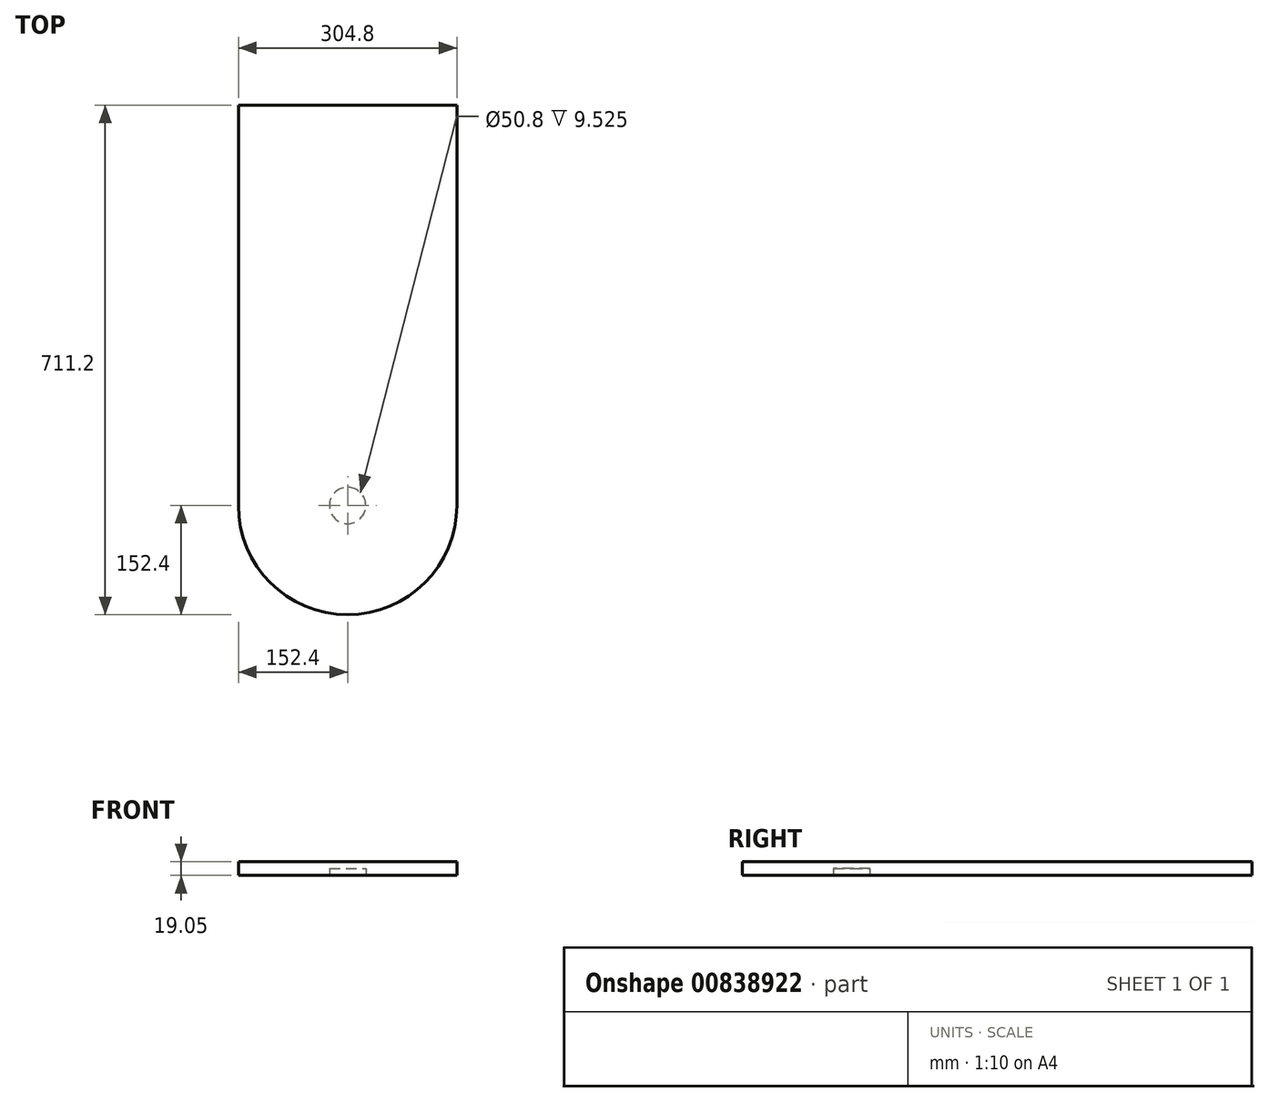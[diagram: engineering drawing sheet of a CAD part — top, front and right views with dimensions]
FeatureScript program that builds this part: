
annotation { "Feature Type Name" : "Feature", "Feature Type Description" : "" }
export const myFeature = defineFeature(function(context is Context, id is Id, definition is map)
    precondition{}
    {
        {
            var Q0;
            Q0=qCreatedBy(makeId("Top.planeOp"),FACE);
            var sketch = newSketch(context, id + "F0", { "sketchPlane" : qUnion([Q0])});
            skLineSegment(sketch, "E0", {"start": v(0, 152.4) * mm, "end": v(0, 711.2) * mm});
            skLineSegment(sketch, "E1", {"start": v(0, 711.2) * mm, "end": v(304.8, 711.2) * mm});
            skLineSegment(sketch, "E2", {"start": v(304.8, 711.2) * mm, "end": v(304.8, 152.4) * mm});
            skArc(sketch, "E3", {"start": v(152.4, 0) * mm, "mid": v(260.16, 44.64) * mm, "end": v(304.8, 152.4) * mm});
            skArc(sketch, "E4", {"start": v(152.4, 0) * mm, "mid": v(44.64, 44.64) * mm, "end": v(0, 152.4) * mm});
            skSolve(sketch);
        }
        {
            var Q0;
            Q0 = qSketchRegion(id + "F0", true);
            extrude(context, id + "F1", {"entities" : qUnion([Q0]), "depth" : 19.05 * mm, "offsetDistance" : 25.4 * mm});
        }
        {
            var Q0;
            Q0=makeQuery(id+"F1.opExtrude","CAP_FACE",FACE,{"disambiguationData":[OSD([sQuery(id+"F0.wireOp",EDGE,"E0"),sQuery(id+"F0.wireOp",EDGE,"E1"),sQuery(id+"F0.wireOp",EDGE,"E2"),sQuery(id+"F0.wireOp",EDGE,"E3"),sQuery(id+"F0.wireOp",EDGE,"E4")])],"isStart":true});
            var sketch = newSketch(context, id + "F2", { "sketchPlane" : qUnion([Q0])});
            skCircle(sketch, "E5", {"center": v(152.4, -152.4) * mm, "radius": 25.4 * mm});
            skSolve(sketch);
        }
        {
            var Q0;
            Q0 = qSketchRegion(id + "F2", true);
            extrude(context, id + "F3", {"entities" : qUnion([Q0]), "operationType" : NewBodyOperationType.REMOVE, "oppositeDirection" : true, "depth" : 9.52 * mm, "offsetDistance" : 25.4 * mm});
        }
    });
